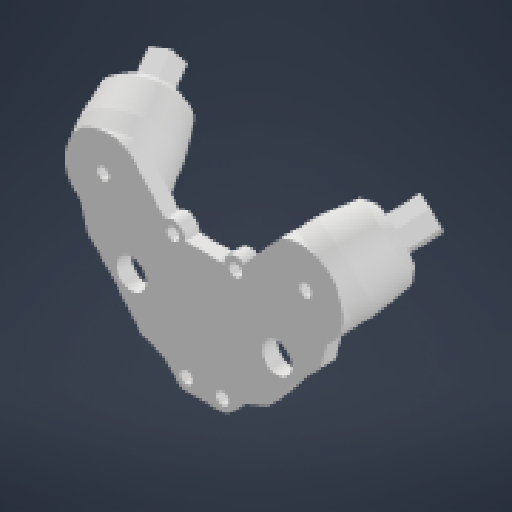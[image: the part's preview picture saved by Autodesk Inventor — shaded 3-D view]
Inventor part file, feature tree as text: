
AUTODESK INVENTOR PART (.ipt)
format: ipt  version: 2024 (Build 280153000, 153)  size: 349,184 bytes
history: native  units: in
note: dims shown in document units (in); Inventor stores cm internally (conversion verified against a paired STEP export)
features: extrude x8, sketch x8, reference x6, chamfer x4, other x4, projected_geometry x3, plane x1, mirror x1
ambient origin geometry x8: Origin, YZ Plane, XZ Plane, XY Plane, X Axis, Y Axis, Z Axis, Center Point
bodies: Solid1 (feature_tree)
feature tree (35):
  extrude  "Extrusion1"  Depth=0.3878in TaperAngle=0.0deg
  plane  "Work Plane1"
  extrude  "Extrusion2"  Depth=0.7087in TaperAngle=0.0deg
  extrude  "Extrusion3"  Depth=0.1969in TaperAngle=45.0deg
  extrude  "Extrusion4"  Depth=0.3937in
  chamfer  "Chamfer1"  Distance=0.1969in
  extrude  "Extrusion5"  Depth=0.1969in TaperAngle=0.0deg
  extrude  "Extrusion6"  Depth=0.1969in TaperAngle=0.0deg
  extrude  "Extrusion7"  Depth=0.0787in
  chamfer  "Chamfer2"  Distance=0.1142in
  chamfer  "Chamfer3"  Distance=0.1654in
  extrude  "Extrusion8"  Depth=0.2756in TaperAngle=0.0deg
  chamfer  "Chamfer4"  Distance=0.0394in
  mirror  "Mirror1"
  sketch  "Sketch1"  dims[d0=0.1969in d1=0.3878in d2=0.0in]
  reference  "Reference1"
  sketch  "Sketch2"  dims[d3=0.4665in d4=0.0in d5=0.7087in d6=0.0in]
  reference  "Reference2"
  sketch  "Sketch3"  dims[d8=0.1969in d9=0.0in d10=0.1142in d11=0.125in d12=45.0deg]
  reference  "Reference3"
  reference  "Reference4"
  sketch  "Sketch4"  dims[d15=0.3937in d16=0.1654in]
  reference  "Reference5"
  reference  "Reference6"
  sketch  "Sketch5"  dims[d17=0.0787in]
  projected_geometry  "Projected Loop1"
  sketch  "Sketch6"  dims[d18=0.2362in]
  sketch  "Sketch7"  dims[d19=0.1654in]
  projected_geometry  "Projected Loop2"
  sketch  "Sketch8"  dims[d20=0.0787in d21=0.1969in d22=0.0in d23=0.1969in d24=0.0in d25=0.1969in d26=0.0in d27=0.5517in d28=0.125in d29=0.055in d30=0.1142in d31=0.125in d32=0.055in d34=0.1654in d35=0.2756in d36=0.0in d37=0.0394in d38=0.125in d39=0.055in d40=0.3937in d41=0.3937in d42=0.0787in d43=0.0in]
  projected_geometry  "Projected Loop3"
  other  "<userpath>\Desktop\Camera_Mount.iam"
  other  "Camera_Mount.iam"
  other  "Universal_Joint:2"
  other  "Universal_Joint_Connector:2"
